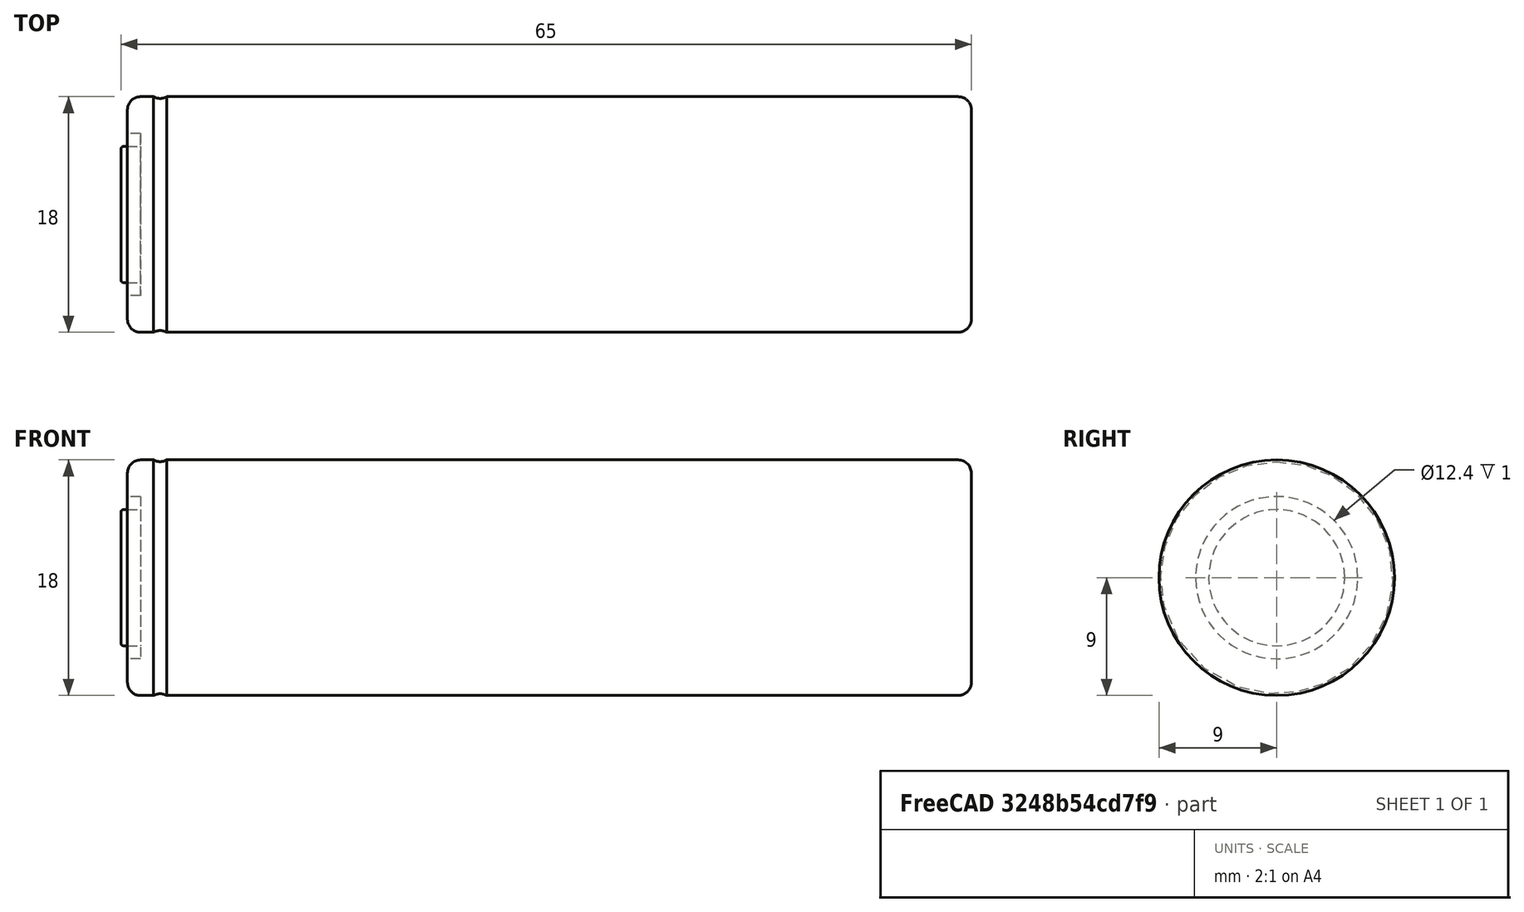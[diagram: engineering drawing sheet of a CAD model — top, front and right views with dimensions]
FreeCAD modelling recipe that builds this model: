
FCSTD DOCUMENT  (FreeCAD 0.19R24291 (Git))
Label: LiIon_18650
License: Creative Commons Attribution-NonCommercial-ShareAlike
LicenseURL: http://creativecommons.org/licenses/by-nc-sa/4.0/
objects: Sketcher::SketchObject×1, PartDesign::Revolution×1, PartDesign::Body×1, PartDesign::CoordinateSystem×1, App::Part×1
note: 5 computed .brp shape members not serialized (recipe doc carries the construction recipe); baked Part::Feature solids carry a one-line shape summary decoded from their .brp

FEATURE [Sketcher::SketchObject] Sketch
  FullyConstrained = true
  MapMode = 5
  Placement = pos=(0,0,0) rot=(1,0,0;1.5708rad)
  Support = -> [XZ_Plane]
  sketch-geometry (13):
    g0: LineSegment StartX=-32.5 StartY=0 StartZ=0 EndX=-32.5 EndY=5 EndZ=0
    g1: ArcOfCircle CenterX=-32.3 CenterY=5 CenterZ=0 NormalX=0 NormalY=0 NormalZ=1 AngleXU=0 Radius=0.2 StartAngle=1.5708 EndAngle=3.14159
    g2: LineSegment StartX=-32.3 StartY=5.2 StartZ=0 EndX=-31 EndY=5.2 EndZ=0
    g3: LineSegment StartX=-31 StartY=5.2 StartZ=0 EndX=-31 EndY=6.2 EndZ=0
    g4: LineSegment StartX=-31 StartY=6.2 StartZ=0 EndX=-32 EndY=6.2 EndZ=0
    g5: LineSegment StartX=-32 StartY=6.2 StartZ=0 EndX=-32 EndY=8 EndZ=0
    g6: ArcOfCircle CenterX=-31 CenterY=8 CenterZ=0 NormalX=0 NormalY=0 NormalZ=1 AngleXU=0 Radius=1 StartAngle=1.5708 EndAngle=3.14159
    g7: LineSegment StartX=-31 StartY=9 StartZ=0 EndX=-30 EndY=9 EndZ=0
    g8: ArcOfCircle CenterX=-29.5 CenterY=9.86603 CenterZ=0 NormalX=0 NormalY=0 NormalZ=1 AngleXU=0 Radius=1 StartAngle=4.18879 EndAngle=5.23599
    g9: LineSegment StartX=-29 StartY=9 StartZ=0 EndX=31.5 EndY=9 EndZ=0
    g10: ArcOfCircle CenterX=31.5 CenterY=8 CenterZ=0 NormalX=0 NormalY=0 NormalZ=1 AngleXU=0 Radius=1 StartAngle=6e-16 EndAngle=1.5708
    g11: LineSegment StartX=32.5 StartY=8 StartZ=0 EndX=32.5 EndY=0 EndZ=0
    g12: LineSegment StartX=32.5 StartY=0 StartZ=0 EndX=-32.5 EndY=0 EndZ=0
  constraints (37):
    c: PointOnObject(g0,g-1)
    c: Vertical(g0)
    c: Tangent(g0,g1) = 1.5708
    c: Tangent(g1,g2) = 1.5708
    c: Coincident(g2,g3)
    c: Vertical(g3)
    c: Coincident(g3,g4)
    c: Horizontal(g4)
    c: Coincident(g4,g5)
    c: Vertical(g5)
    c: Tangent(g5,g6) = 1.5708
    c: Horizontal(g7)
    c: Coincident(g8,g9)
    c: Horizontal(g9)
    c: Tangent(g9,g10) = 1.5708
    c: Tangent(g10,g11) = 1.5708
    c: Coincident(g11,g12)
    c: Coincident(g12,g0)
    c: Horizontal(g12)
    c: Coincident(g7,g8)
    c: Horizontal(g8,g7)
    c: Vertical(g11)
    c: Horizontal(g2)
    c: Radius(g10) = 1
    c: Radius(g6) = 1
    c: Radius(g1) = 0.2
    c: Distance(g-1,g9) = 9
    c: Radius(g8) = 1
    c: Distance(g0) = 5
    c: Distance(g3) = 1
    c: Tangent(g6,g7) = 1.5708
    c: Distance(g7) = 1
    c: DistanceX(g7,g8) = 1
    c: Distance(g12) = 65
    c: Distance(g-1,g11) = 32.5
    c: Distance(g4) = 1
    c: Distance(g4,g0) = 0.5
FEATURE [PartDesign::Revolution] Revolution
  Angle = 360
  Axis = (1,0,0)
  Base = (0,0,0)
  Placement = pos=(0,0,0) rot=(1,0,0;1.5708rad)
  Profile = -> Sketch
  ReferenceAxis = -> X_Axis
  Refine = true
FEATURE [PartDesign::Body] Body
  Group = -> [Sketch,Revolution]
  Origin = -> Origin
  Tip = -> Revolution
FEATURE [PartDesign::CoordinateSystem] LCS_0  label="LCS_Battery_Origin"
  AttacherType = Attacher::AttachEngine3D
  MapMode = 2
  Support = -> [X_Axis001]
FEATURE [App::Part] _8650  label="18650"
  Group = -> [LCS_0,Body]
  Origin = -> Origin001
